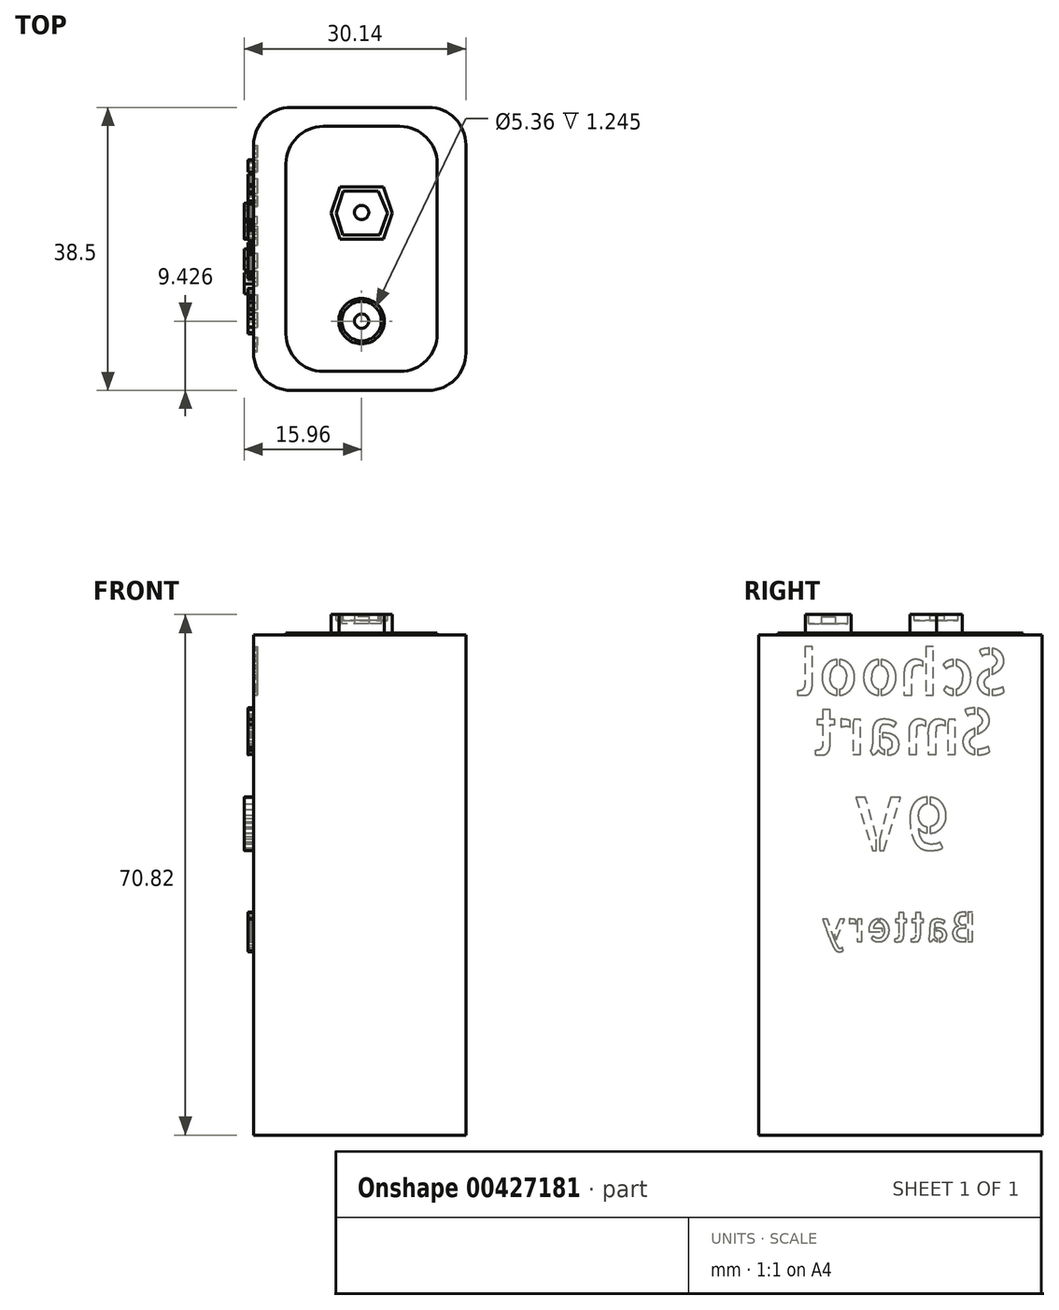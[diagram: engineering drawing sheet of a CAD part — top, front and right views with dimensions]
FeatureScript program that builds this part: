
annotation { "Feature Type Name" : "Feature", "Feature Type Description" : "" }
export const myFeature = defineFeature(function(context is Context, id is Id, definition is map)
    precondition{}
    {
        {
            var Q0;
            Q0=qCreatedBy(makeId("Top.planeOp"),FACE);
            var sketch = newSketch(context, id + "F0", { "sketchPlane" : qUnion([Q0])});
            skLineSegment(sketch, "E0.bottom", {"start": v(-14.18, 19.25) * mm, "end": v(14.18, 19.25) * mm});
            skLineSegment(sketch, "E0.top", {"start": v(-14.18, -19.25) * mm, "end": v(14.18, -19.25) * mm});
            skLineSegment(sketch, "E0.left", {"start": v(-14.18, 19.25) * mm, "end": v(-14.18, -19.25) * mm});
            skLineSegment(sketch, "E0.right", {"start": v(14.18, 19.25) * mm, "end": v(14.18, -19.25) * mm});
            skPoint(sketch, "E0.middle", {"position": v(0, 0) * mm});
            skSolve(sketch);
        }
        {
            var Q0;
            Q0=makeQuery(id+"F0.imprint","IMPRINT",FACE,{"disambiguationData":[TD([[makeQuery(id+"F0.imprint","IMPRINT",EDGE,{"derivedFrom":sQuery(id+"F0.wireOp",EDGE,"E0.bottom")}),-1.0]])]});
            extrude(context, id + "F1", {"entities" : qUnion([Q0]), "depth" : 68.07 * mm});
        }
        {
            var Q0;
            Q0=makeQuery(id+"F1.opExtrude","CAP_FACE",FACE,{"disambiguationData":[OSD([sQuery(id+"F0.wireOp",EDGE,"E0.bottom"),sQuery(id+"F0.wireOp",EDGE,"E0.top"),sQuery(id+"F0.wireOp",EDGE,"E0.left"),sQuery(id+"F0.wireOp",EDGE,"E0.right")])],"isStart":false});
            var sketch = newSketch(context, id + "F2", { "sketchPlane" : qUnion([Q0])});
            skLineSegment(sketch, "E1", {"start": v(0, 8.42) * mm, "end": v(-2.94, 8.42) * mm});
            skLineSegment(sketch, "E2", {"start": v(0, 8.42) * mm, "end": v(2.94, 8.42) * mm});
            skLineSegment(sketch, "E3", {"start": v(2.94, 8.42) * mm, "end": v(4.16, 4.9) * mm});
            skLineSegment(sketch, "E4", {"start": v(4.16, 4.9) * mm, "end": v(2.94, 1.33) * mm});
            skLineSegment(sketch, "E5", {"start": v(2.94, 1.33) * mm, "end": v(-2.94, 1.33) * mm});
            skLineSegment(sketch, "E6", {"start": v(-2.94, 1.33) * mm, "end": v(-4.16, 4.9) * mm});
            skLineSegment(sketch, "E7", {"start": v(-4.16, 4.9) * mm, "end": v(-2.94, 8.42) * mm});
            skSolve(sketch);
        }
        {
            var Q0;
            Q0=makeQuery(id+"F2.imprint","IMPRINT",FACE,{"disambiguationData":[TD([[makeQuery(id+"F2.imprint","IMPRINT",EDGE,{"derivedFrom":sQuery(id+"F2.wireOp",EDGE,"E1")}),1.0]])]});
            extrude(context, id + "F3", {"entities" : qUnion([Q0]), "operationType" : NewBodyOperationType.ADD, "depth" : 2.74 * mm});
        }
        {
            var Q0;
            Q0=makeQuery(id+"F3.opExtrude","CAP_FACE",FACE,{"disambiguationData":[OSD([sQuery(id+"F2.wireOp",EDGE,"E1"),sQuery(id+"F2.wireOp",EDGE,"E2"),sQuery(id+"F2.wireOp",EDGE,"E3"),sQuery(id+"F2.wireOp",EDGE,"E4"),sQuery(id+"F2.wireOp",EDGE,"E5"),sQuery(id+"F2.wireOp",EDGE,"E6"),sQuery(id+"F2.wireOp",EDGE,"E7")])],"isStart":false});
            var sketch = newSketch(context, id + "F4", { "sketchPlane" : qUnion([Q0])});
            skLineSegment(sketch, "E8", {"start": v(3.55, 4.9) * mm, "end": v(2.26, 7.85) * mm});
            skPoint(sketch, "E8.startSnap0", {"position": v(3.55, 6.66) * mm});
            skLineSegment(sketch, "E9", {"start": v(2.26, 7.85) * mm, "end": v(-2.5, 7.85) * mm});
            skLineSegment(sketch, "E10", {"start": v(-2.5, 7.85) * mm, "end": v(-3.49, 4.9) * mm});
            skLineSegment(sketch, "E11", {"start": v(-3.49, 4.9) * mm, "end": v(-2.6, 1.88) * mm});
            skLineSegment(sketch, "E12", {"start": v(-2.6, 1.88) * mm, "end": v(2.48, 1.88) * mm});
            skLineSegment(sketch, "E13", {"start": v(2.48, 1.88) * mm, "end": v(3.55, 4.9) * mm});
            skSolve(sketch);
        }
        {
            var Q0;
            Q0=makeQuery(id+"F4.imprint","IMPRINT",FACE,{"disambiguationData":[TD([[makeQuery(id+"F4.imprint","IMPRINT",EDGE,{"derivedFrom":sQuery(id+"F4.wireOp",EDGE,"E8")}),1.0]])]});
            extrude(context, id + "F5", {"entities" : qUnion([Q0]), "operationType" : NewBodyOperationType.REMOVE, "oppositeDirection" : true, "depth" : 1.07 * mm});
        }
        {
            var Q0;
            Q0=makeQuery(id+"F2.imprint","IMPRINT",FACE,{"disambiguationData":[TD([[makeQuery(id+"F2.imprint","IMPRINT",EDGE,{"derivedFrom":sQuery(id+"F2.wireOp",EDGE,"E1")}),-1.0]])]});
            var sketch = newSketch(context, id + "F6", { "sketchPlane" : qUnion([Q0])});
            skCircle(sketch, "E14", {"center": v(0, -9.82) * mm, "radius": 3.1 * mm});
            skSolve(sketch);
        }
        {
            var Q0;
            Q0=makeQuery(id+"F6.imprint","IMPRINT",FACE,{"disambiguationData":[TD([[makeQuery(id+"F6.imprint","IMPRINT",EDGE,{"derivedFrom":sQuery(id+"F6.wireOp",EDGE,"E14")}),1.0]])]});
            var Q1;
            Q1=sQuery(id+"F6.wireOp",EDGE,"E14");
            extrude(context, id + "F7", {"entities" : qUnion([Q0]), "operationType" : NewBodyOperationType.ADD, "surfaceEntities" : qUnion([Q1]), "depth" : 2.74 * mm});
        }
        {
            var Q0;
            Q0=makeQuery(id+"F7.opExtrude","CAP_FACE",FACE,{"disambiguationData":[OSD([sQuery(id+"F6.wireOp",EDGE,"E14")])],"isStart":false});
            var sketch = newSketch(context, id + "F8", { "sketchPlane" : qUnion([Q0])});
            skCircle(sketch, "E15", {"center": v(0, -9.82) * mm, "radius": 2.68 * mm});
            skSolve(sketch);
        }
        {
            var Q0;
            Q0=makeQuery(id+"F8.imprint","IMPRINT",FACE,{"disambiguationData":[TD([[makeQuery(id+"F8.imprint","IMPRINT",EDGE,{"derivedFrom":sQuery(id+"F8.wireOp",EDGE,"E15")}),1.0]])]});
            extrude(context, id + "F9", {"entities" : qUnion([Q0]), "operationType" : NewBodyOperationType.REMOVE, "oppositeDirection" : true, "depth" : 1.24 * mm});
        }
        {
            var Q0;
            Q0=makeQuery(id+"F9.boolean.opBoolean","COPY",FACE,{"derivedFrom":makeQuery(id+"F9.opExtrude","CAP_FACE",FACE,{"disambiguationData":[OSD([sQuery(id+"F8.wireOp",EDGE,"E15")])],"isStart":false})});
            var sketch = newSketch(context, id + "F10", { "sketchPlane" : qUnion([Q0])});
            skCircle(sketch, "E16", {"center": v(0, -9.82) * mm, "radius": 0.97 * mm});
            skSolve(sketch);
        }
        {
            var Q0;
            Q0=makeQuery(id+"F10.imprint","IMPRINT",FACE,{"disambiguationData":[TD([[makeQuery(id+"F10.imprint","IMPRINT",EDGE,{"derivedFrom":sQuery(id+"F10.wireOp",EDGE,"E16")}),1.0]])]});
            extrude(context, id + "F11", {"entities" : qUnion([Q0]), "operationType" : NewBodyOperationType.ADD, "depth" : 0.94 * mm});
        }
        {
            var Q0;
            Q0=makeQuery(id+"F5.boolean.opBoolean","COPY",FACE,{"derivedFrom":makeQuery(id+"F5.opExtrude","CAP_FACE",FACE,{"disambiguationData":[OSD([sQuery(id+"F4.wireOp",EDGE,"E8"),sQuery(id+"F4.wireOp",EDGE,"E9"),sQuery(id+"F4.wireOp",EDGE,"E10"),sQuery(id+"F4.wireOp",EDGE,"E11"),sQuery(id+"F4.wireOp",EDGE,"E12"),sQuery(id+"F4.wireOp",EDGE,"E13")])],"isStart":false})});
            var sketch = newSketch(context, id + "F12", { "sketchPlane" : qUnion([Q0])});
            skCircle(sketch, "E17", {"center": v(0, 4.96) * mm, "radius": 0.97 * mm});
            skSolve(sketch);
        }
        {
            var Q0;
            Q0=makeQuery(id+"F12.imprint","IMPRINT",FACE,{"disambiguationData":[TD([[makeQuery(id+"F12.imprint","IMPRINT",EDGE,{"derivedFrom":sQuery(id+"F12.wireOp",EDGE,"E17")}),1.0]])]});
            extrude(context, id + "F13", {"entities" : qUnion([Q0]), "operationType" : NewBodyOperationType.ADD, "depth" : 0.94 * mm});
        }
        {
            var Q0;
            Q0=makeQuery(id+"F1.opExtrude","SWEPT_FACE",FACE,{"disambiguationData":[OSD([sQuery(id+"F0.wireOp",EDGE,"E0.left")])]});
            var sketch = newSketch(context, id + "F14", { "sketchPlane" : qUnion([Q0])});
            skText(sketch, "E18", { "text": "School", "fontName": "AllertaStencil-Regular.ttf"});
            const initialGuessF14  = {"E18": [-0.0148, 0.05987, 1, 0, 0.00628]};
            skSetInitialGuess(sketch, initialGuessF14);
            skSolve(sketch);
        }
        {
            var Q0;
            Q0=makeQuery(id+"F14.imprint","IMPRINT",FACE,{"disambiguationData":[TD([[makeQuery(id+"F14.imprint","IMPRINT",EDGE,{"derivedFrom":sQuery(id+"F14.wireOp",EDGE,"E18.sketch_text.stroke-0")}),1.0]])]});
            extrude(context, id + "F15", {"entities" : qUnion([Q0]), "operationType" : NewBodyOperationType.ADD, "depth" : 0.5 * mm});
        }
        {
            var Q0;
            Q0=makeQuery(id+"F15.opExtrude","CAP_FACE",FACE,{"disambiguationData":[OSD([sQuery(id+"F0.wireOp",EDGE,"E0.bottom"),sQuery(id+"F0.wireOp",EDGE,"E0.top"),sQuery(id+"F0.wireOp",EDGE,"E0.left"),sQuery(id+"F14.wireOp",EDGE,"E18.sketch_text.stroke-0"),sQuery(id+"F14.wireOp",EDGE,"E18.sketch_text.stroke-1"),sQuery(id+"F14.wireOp",EDGE,"E18.sketch_text.stroke-2"),sQuery(id+"F14.wireOp",EDGE,"E18.sketch_text.stroke-3"),sQuery(id+"F14.wireOp",EDGE,"E18.sketch_text.stroke-4"),sQuery(id+"F14.wireOp",EDGE,"E18.sketch_text.stroke-5"),sQuery(id+"F14.wireOp",EDGE,"E18.sketch_text.stroke-6"),sQuery(id+"F14.wireOp",EDGE,"E18.sketch_text.stroke-7"),sQuery(id+"F14.wireOp",EDGE,"E18.sketch_text.stroke-8"),sQuery(id+"F14.wireOp",EDGE,"E18.sketch_text.stroke-9"),sQuery(id+"F14.wireOp",EDGE,"E18.sketch_text.stroke-10"),sQuery(id+"F14.wireOp",EDGE,"E18.sketch_text.stroke-11"),sQuery(id+"F14.wireOp",EDGE,"E18.sketch_text.stroke-12"),sQuery(id+"F14.wireOp",EDGE,"E18.sketch_text.stroke-13"),sQuery(id+"F14.wireOp",EDGE,"E18.sketch_text.stroke-14"),sQuery(id+"F14.wireOp",EDGE,"E18.sketch_text.stroke-15"),sQuery(id+"F14.wireOp",EDGE,"E18.sketch_text.stroke-16"),sQuery(id+"F14.wireOp",EDGE,"E18.sketch_text.stroke-17"),sQuery(id+"F14.wireOp",EDGE,"E18.sketch_text.stroke-18"),sQuery(id+"F14.wireOp",EDGE,"E18.sketch_text.stroke-19"),sQuery(id+"F14.wireOp",EDGE,"E18.sketch_text.stroke-20"),sQuery(id+"F14.wireOp",EDGE,"E18.sketch_text.stroke-21"),sQuery(id+"F14.wireOp",EDGE,"E18.sketch_text.stroke-22"),sQuery(id+"F14.wireOp",EDGE,"E18.sketch_text.stroke-23"),sQuery(id+"F14.wireOp",EDGE,"E18.sketch_text.stroke-24"),sQuery(id+"F14.wireOp",EDGE,"E18.sketch_text.stroke-25"),sQuery(id+"F14.wireOp",EDGE,"E18.sketch_text.stroke-26"),sQuery(id+"F14.wireOp",EDGE,"E18.sketch_text.stroke-27"),sQuery(id+"F14.wireOp",EDGE,"E18.sketch_text.stroke-28"),sQuery(id+"F14.wireOp",EDGE,"E18.sketch_text.stroke-29"),sQuery(id+"F14.wireOp",EDGE,"E18.sketch_text.stroke-30"),sQuery(id+"F14.wireOp",EDGE,"E18.sketch_text.stroke-31"),sQuery(id+"F14.wireOp",EDGE,"E18.sketch_text.stroke-32"),sQuery(id+"F14.wireOp",EDGE,"E18.sketch_text.stroke-33"),sQuery(id+"F14.wireOp",EDGE,"E18.sketch_text.stroke-34"),sQuery(id+"F14.wireOp",EDGE,"E18.sketch_text.stroke-35"),sQuery(id+"F14.wireOp",EDGE,"E18.sketch_text.stroke-36"),sQuery(id+"F14.wireOp",EDGE,"E18.sketch_text.stroke-37"),sQuery(id+"F14.wireOp",EDGE,"E18.sketch_text.stroke-38"),sQuery(id+"F14.wireOp",EDGE,"E18.sketch_text.stroke-39"),sQuery(id+"F14.wireOp",EDGE,"E18.sketch_text.stroke-40"),sQuery(id+"F14.wireOp",EDGE,"E18.sketch_text.stroke-41"),sQuery(id+"F14.wireOp",EDGE,"E18.sketch_text.stroke-42"),sQuery(id+"F14.wireOp",EDGE,"E18.sketch_text.stroke-43"),sQuery(id+"F14.wireOp",EDGE,"E18.sketch_text.stroke-44"),sQuery(id+"F14.wireOp",EDGE,"E18.sketch_text.stroke-45"),sQuery(id+"F14.wireOp",EDGE,"E18.sketch_text.stroke-46"),sQuery(id+"F14.wireOp",EDGE,"E18.sketch_text.stroke-47"),sQuery(id+"F14.wireOp",EDGE,"E18.sketch_text.stroke-48"),sQuery(id+"F14.wireOp",EDGE,"E18.sketch_text.stroke-49"),sQuery(id+"F14.wireOp",EDGE,"E18.sketch_text.stroke-50"),sQuery(id+"F14.wireOp",EDGE,"E18.sketch_text.stroke-51"),sQuery(id+"F14.wireOp",EDGE,"E18.sketch_text.stroke-52"),sQuery(id+"F14.wireOp",EDGE,"E18.sketch_text.stroke-53"),sQuery(id+"F14.wireOp",EDGE,"E18.sketch_text.stroke-54"),sQuery(id+"F14.wireOp",EDGE,"E18.sketch_text.stroke-55"),sQuery(id+"F14.wireOp",EDGE,"E18.sketch_text.stroke-56"),sQuery(id+"F14.wireOp",EDGE,"E18.sketch_text.stroke-57"),sQuery(id+"F14.wireOp",EDGE,"E18.sketch_text.stroke-58"),sQuery(id+"F14.wireOp",EDGE,"E18.sketch_text.stroke-59"),sQuery(id+"F14.wireOp",EDGE,"E18.sketch_text.stroke-60"),sQuery(id+"F14.wireOp",EDGE,"E18.sketch_text.stroke-61"),sQuery(id+"F14.wireOp",EDGE,"E18.sketch_text.stroke-62"),sQuery(id+"F14.wireOp",EDGE,"E18.sketch_text.stroke-63"),sQuery(id+"F14.wireOp",EDGE,"E18.sketch_text.stroke-64"),sQuery(id+"F14.wireOp",EDGE,"E18.sketch_text.stroke-65"),sQuery(id+"F14.wireOp",EDGE,"E18.sketch_text.stroke-66"),sQuery(id+"F14.wireOp",EDGE,"E18.sketch_text.stroke-67"),sQuery(id+"F14.wireOp",EDGE,"E18.sketch_text.stroke-68"),sQuery(id+"F14.wireOp",EDGE,"E18.sketch_text.stroke-69"),sQuery(id+"F14.wireOp",EDGE,"E18.sketch_text.stroke-70"),sQuery(id+"F14.wireOp",EDGE,"E18.sketch_text.stroke-71"),sQuery(id+"F14.wireOp",EDGE,"E18.sketch_text.stroke-72"),sQuery(id+"F14.wireOp",EDGE,"E18.sketch_text.stroke-73"),sQuery(id+"F14.wireOp",EDGE,"E18.sketch_text.stroke-74"),sQuery(id+"F14.wireOp",EDGE,"E18.sketch_text.stroke-75"),sQuery(id+"F14.wireOp",EDGE,"E18.sketch_text.stroke-76"),sQuery(id+"F14.wireOp",EDGE,"E18.sketch_text.stroke-77"),sQuery(id+"F14.wireOp",EDGE,"E18.sketch_text.stroke-78"),sQuery(id+"F14.wireOp",EDGE,"E18.sketch_text.stroke-79"),sQuery(id+"F14.wireOp",EDGE,"E18.sketch_text.stroke-80"),sQuery(id+"F14.wireOp",EDGE,"E18.sketch_text.stroke-81"),sQuery(id+"F14.wireOp",EDGE,"E18.sketch_text.stroke-82"),sQuery(id+"F14.wireOp",EDGE,"E18.sketch_text.stroke-83"),sQuery(id+"F14.wireOp",EDGE,"E18.sketch_text.stroke-84"),sQuery(id+"F14.wireOp",EDGE,"E18.sketch_text.stroke-85"),sQuery(id+"F14.wireOp",EDGE,"E18.sketch_text.stroke-86"),sQuery(id+"F14.wireOp",EDGE,"E18.sketch_text.stroke-87"),sQuery(id+"F14.wireOp",EDGE,"E18.sketch_text.stroke-88"),sQuery(id+"F14.wireOp",EDGE,"E18.sketch_text.stroke-89"),sQuery(id+"F14.wireOp",EDGE,"E18.sketch_text.stroke-90"),sQuery(id+"F14.wireOp",EDGE,"E18.sketch_text.stroke-91"),sQuery(id+"F14.wireOp",EDGE,"E18.sketch_text.stroke-92"),sQuery(id+"F14.wireOp",EDGE,"E18.sketch_text.stroke-93"),sQuery(id+"F14.wireOp",EDGE,"E18.sketch_text.stroke-94"),sQuery(id+"F14.wireOp",EDGE,"E18.sketch_text.stroke-95"),sQuery(id+"F14.wireOp",EDGE,"E18.sketch_text.stroke-96"),sQuery(id+"F14.wireOp",EDGE,"E18.sketch_text.stroke-97"),sQuery(id+"F14.wireOp",EDGE,"E18.sketch_text.stroke-98"),sQuery(id+"F14.wireOp",EDGE,"E18.sketch_text.stroke-99"),sQuery(id+"F14.wireOp",EDGE,"E18.sketch_text.stroke-100"),sQuery(id+"F14.wireOp",EDGE,"E18.sketch_text.stroke-101"),sQuery(id+"F14.wireOp",EDGE,"E18.sketch_text.stroke-102"),sQuery(id+"F14.wireOp",EDGE,"E18.sketch_text.stroke-103"),sQuery(id+"F14.wireOp",EDGE,"E18.sketch_text.stroke-104"),sQuery(id+"F14.wireOp",EDGE,"E18.sketch_text.stroke-105"),sQuery(id+"F14.wireOp",EDGE,"E18.sketch_text.stroke-106"),sQuery(id+"F14.wireOp",EDGE,"E18.sketch_text.stroke-107"),sQuery(id+"F14.wireOp",EDGE,"E18.sketch_text.stroke-108"),sQuery(id+"F14.wireOp",EDGE,"E18.sketch_text.stroke-109"),sQuery(id+"F14.wireOp",EDGE,"E18.sketch_text.stroke-110"),sQuery(id+"F14.wireOp",EDGE,"E18.sketch_text.stroke-111"),sQuery(id+"F14.wireOp",EDGE,"E18.sketch_text.stroke-112"),sQuery(id+"F14.wireOp",EDGE,"E18.sketch_text.stroke-113"),sQuery(id+"F14.wireOp",EDGE,"E18.sketch_text.stroke-114"),sQuery(id+"F14.wireOp",EDGE,"E18.sketch_text.stroke-115"),sQuery(id+"F14.wireOp",EDGE,"E18.sketch_text.stroke-116"),sQuery(id+"F14.wireOp",EDGE,"E18.sketch_text.stroke-117"),sQuery(id+"F14.wireOp",EDGE,"E18.sketch_text.stroke-118"),sQuery(id+"F14.wireOp",EDGE,"E18.sketch_text.stroke-119"),sQuery(id+"F14.wireOp",EDGE,"E18.sketch_text.stroke-120"),sQuery(id+"F14.wireOp",EDGE,"E18.sketch_text.stroke-121"),sQuery(id+"F14.wireOp",EDGE,"E18.sketch_text.stroke-122"),sQuery(id+"F14.wireOp",EDGE,"E18.sketch_text.stroke-123"),sQuery(id+"F14.wireOp",EDGE,"E18.sketch_text.stroke-124"),sQuery(id+"F14.wireOp",EDGE,"E18.sketch_text.stroke-125"),sQuery(id+"F14.wireOp",EDGE,"E18.sketch_text.stroke-126"),sQuery(id+"F14.wireOp",EDGE,"E18.sketch_text.stroke-127"),sQuery(id+"F14.wireOp",EDGE,"E18.sketch_text.stroke-128"),sQuery(id+"F14.wireOp",EDGE,"E18.sketch_text.stroke-129"),sQuery(id+"F14.wireOp",EDGE,"E18.sketch_text.stroke-130"),sQuery(id+"F14.wireOp",EDGE,"E18.sketch_text.stroke-131"),sQuery(id+"F14.wireOp",EDGE,"E18.sketch_text.stroke-132"),sQuery(id+"F14.wireOp",EDGE,"E18.sketch_text.stroke-133"),sQuery(id+"F14.wireOp",EDGE,"E18.sketch_text.stroke-134"),sQuery(id+"F14.wireOp",EDGE,"E18.sketch_text.stroke-135"),sQuery(id+"F14.wireOp",EDGE,"E18.sketch_text.stroke-136"),sQuery(id+"F14.wireOp",EDGE,"E18.sketch_text.stroke-137"),sQuery(id+"F14.wireOp",EDGE,"E18.sketch_text.stroke-138"),sQuery(id+"F14.wireOp",EDGE,"E18.sketch_text.stroke-139"),sQuery(id+"F14.wireOp",EDGE,"E18.sketch_text.stroke-140"),sQuery(id+"F14.wireOp",EDGE,"E18.sketch_text.stroke-141"),sQuery(id+"F14.wireOp",EDGE,"E18.sketch_text.stroke-142"),sQuery(id+"F14.wireOp",EDGE,"E18.sketch_text.stroke-143"),sQuery(id+"F14.wireOp",EDGE,"E18.sketch_text.stroke-144"),sQuery(id+"F14.wireOp",EDGE,"E18.sketch_text.stroke-145"),sQuery(id+"F14.wireOp",EDGE,"E18.sketch_text.stroke-146"),sQuery(id+"F14.wireOp",EDGE,"E18.sketch_text.stroke-147"),sQuery(id+"F14.wireOp",EDGE,"E18.sketch_text.stroke-148"),sQuery(id+"F14.wireOp",EDGE,"E18.sketch_text.stroke-149"),sQuery(id+"F14.wireOp",EDGE,"E18.sketch_text.stroke-150"),sQuery(id+"F14.wireOp",EDGE,"E18.sketch_text.stroke-151"),sQuery(id+"F14.wireOp",EDGE,"E18.sketch_text.stroke-152"),sQuery(id+"F14.wireOp",EDGE,"E18.sketch_text.stroke-153"),sQuery(id+"F14.wireOp",EDGE,"E18.sketch_text.stroke-154"),sQuery(id+"F14.wireOp",EDGE,"E18.sketch_text.stroke-155"),sQuery(id+"F14.wireOp",EDGE,"E18.sketch_text.stroke-156"),sQuery(id+"F14.wireOp",EDGE,"E18.sketch_text.stroke-157"),sQuery(id+"F14.wireOp",EDGE,"E18.sketch_text.stroke-158"),sQuery(id+"F14.wireOp",EDGE,"E18.sketch_text.stroke-159"),sQuery(id+"F14.wireOp",EDGE,"E18.sketch_text.stroke-160"),sQuery(id+"F14.wireOp",EDGE,"E18.sketch_text.stroke-161"),sQuery(id+"F14.wireOp",EDGE,"E18.sketch_text.stroke-162"),sQuery(id+"F14.wireOp",EDGE,"E18.sketch_text.stroke-163"),sQuery(id+"F14.wireOp",EDGE,"E18.sketch_text.stroke-164"),sQuery(id+"F14.wireOp",EDGE,"E18.sketch_text.stroke-165"),sQuery(id+"F14.wireOp",EDGE,"E18.sketch_text.stroke-166"),sQuery(id+"F14.wireOp",EDGE,"E18.sketch_text.stroke-167"),sQuery(id+"F14.wireOp",EDGE,"E18.sketch_text.stroke-168"),sQuery(id+"F14.wireOp",EDGE,"E18.sketch_text.stroke-169"),sQuery(id+"F14.wireOp",EDGE,"E18.sketch_text.stroke-170"),sQuery(id+"F14.wireOp",EDGE,"E18.sketch_text.stroke-171"),sQuery(id+"F14.wireOp",EDGE,"E18.sketch_text.stroke-172"),sQuery(id+"F14.wireOp",EDGE,"E18.sketch_text.stroke-173"),sQuery(id+"F14.wireOp",EDGE,"E18.sketch_text.stroke-174"),sQuery(id+"F14.wireOp",EDGE,"E18.sketch_text.stroke-175"),sQuery(id+"F14.wireOp",EDGE,"E18.sketch_text.stroke-176"),sQuery(id+"F14.wireOp",EDGE,"E18.sketch_text.stroke-177"),sQuery(id+"F14.wireOp",EDGE,"E18.sketch_text.stroke-178"),sQuery(id+"F14.wireOp",EDGE,"E18.sketch_text.stroke-179"),sQuery(id+"F14.wireOp",EDGE,"E18.sketch_text.stroke-180"),sQuery(id+"F14.wireOp",EDGE,"E18.sketch_text.stroke-181"),sQuery(id+"F14.wireOp",EDGE,"E18.sketch_text.stroke-182")])],"isStart":false});
            var sketch = newSketch(context, id + "F16", { "sketchPlane" : qUnion([Q0])});
            skText(sketch, "E19", { "text": "Smart", "fontName": "AllertaStencil-Regular.ttf"});
            const initialGuessF16  = {"E19": [-0.01282, 0.05176, 1, 0, 0.00627]};
            skSetInitialGuess(sketch, initialGuessF16);
            skSolve(sketch);
        }
        {
            var Q0;
            Q0 = qSketchRegion(id + "F16", true);
            extrude(context, id + "F17", {"entities" : qUnion([Q0]), "operationType" : NewBodyOperationType.ADD, "depth" : 0.76 * mm});
        }
        {
            var Q0;
            Q0=makeQuery(id+"F15.opExtrude","CAP_FACE",FACE,{"disambiguationData":[OSD([sQuery(id+"F0.wireOp",EDGE,"E0.bottom"),sQuery(id+"F0.wireOp",EDGE,"E0.top"),sQuery(id+"F0.wireOp",EDGE,"E0.left"),sQuery(id+"F14.wireOp",EDGE,"E18.sketch_text.stroke-0"),sQuery(id+"F14.wireOp",EDGE,"E18.sketch_text.stroke-1"),sQuery(id+"F14.wireOp",EDGE,"E18.sketch_text.stroke-2"),sQuery(id+"F14.wireOp",EDGE,"E18.sketch_text.stroke-3"),sQuery(id+"F14.wireOp",EDGE,"E18.sketch_text.stroke-4"),sQuery(id+"F14.wireOp",EDGE,"E18.sketch_text.stroke-5"),sQuery(id+"F14.wireOp",EDGE,"E18.sketch_text.stroke-6"),sQuery(id+"F14.wireOp",EDGE,"E18.sketch_text.stroke-7"),sQuery(id+"F14.wireOp",EDGE,"E18.sketch_text.stroke-8"),sQuery(id+"F14.wireOp",EDGE,"E18.sketch_text.stroke-9"),sQuery(id+"F14.wireOp",EDGE,"E18.sketch_text.stroke-10"),sQuery(id+"F14.wireOp",EDGE,"E18.sketch_text.stroke-11"),sQuery(id+"F14.wireOp",EDGE,"E18.sketch_text.stroke-12"),sQuery(id+"F14.wireOp",EDGE,"E18.sketch_text.stroke-13"),sQuery(id+"F14.wireOp",EDGE,"E18.sketch_text.stroke-14"),sQuery(id+"F14.wireOp",EDGE,"E18.sketch_text.stroke-15"),sQuery(id+"F14.wireOp",EDGE,"E18.sketch_text.stroke-16"),sQuery(id+"F14.wireOp",EDGE,"E18.sketch_text.stroke-17"),sQuery(id+"F14.wireOp",EDGE,"E18.sketch_text.stroke-18"),sQuery(id+"F14.wireOp",EDGE,"E18.sketch_text.stroke-19"),sQuery(id+"F14.wireOp",EDGE,"E18.sketch_text.stroke-20"),sQuery(id+"F14.wireOp",EDGE,"E18.sketch_text.stroke-21"),sQuery(id+"F14.wireOp",EDGE,"E18.sketch_text.stroke-22"),sQuery(id+"F14.wireOp",EDGE,"E18.sketch_text.stroke-23"),sQuery(id+"F14.wireOp",EDGE,"E18.sketch_text.stroke-24"),sQuery(id+"F14.wireOp",EDGE,"E18.sketch_text.stroke-25"),sQuery(id+"F14.wireOp",EDGE,"E18.sketch_text.stroke-26"),sQuery(id+"F14.wireOp",EDGE,"E18.sketch_text.stroke-27"),sQuery(id+"F14.wireOp",EDGE,"E18.sketch_text.stroke-28"),sQuery(id+"F14.wireOp",EDGE,"E18.sketch_text.stroke-29"),sQuery(id+"F14.wireOp",EDGE,"E18.sketch_text.stroke-30"),sQuery(id+"F14.wireOp",EDGE,"E18.sketch_text.stroke-31"),sQuery(id+"F14.wireOp",EDGE,"E18.sketch_text.stroke-32"),sQuery(id+"F14.wireOp",EDGE,"E18.sketch_text.stroke-33"),sQuery(id+"F14.wireOp",EDGE,"E18.sketch_text.stroke-34"),sQuery(id+"F14.wireOp",EDGE,"E18.sketch_text.stroke-35"),sQuery(id+"F14.wireOp",EDGE,"E18.sketch_text.stroke-36"),sQuery(id+"F14.wireOp",EDGE,"E18.sketch_text.stroke-37"),sQuery(id+"F14.wireOp",EDGE,"E18.sketch_text.stroke-38"),sQuery(id+"F14.wireOp",EDGE,"E18.sketch_text.stroke-39"),sQuery(id+"F14.wireOp",EDGE,"E18.sketch_text.stroke-40"),sQuery(id+"F14.wireOp",EDGE,"E18.sketch_text.stroke-41"),sQuery(id+"F14.wireOp",EDGE,"E18.sketch_text.stroke-42"),sQuery(id+"F14.wireOp",EDGE,"E18.sketch_text.stroke-43"),sQuery(id+"F14.wireOp",EDGE,"E18.sketch_text.stroke-44"),sQuery(id+"F14.wireOp",EDGE,"E18.sketch_text.stroke-45"),sQuery(id+"F14.wireOp",EDGE,"E18.sketch_text.stroke-46"),sQuery(id+"F14.wireOp",EDGE,"E18.sketch_text.stroke-47"),sQuery(id+"F14.wireOp",EDGE,"E18.sketch_text.stroke-48"),sQuery(id+"F14.wireOp",EDGE,"E18.sketch_text.stroke-49"),sQuery(id+"F14.wireOp",EDGE,"E18.sketch_text.stroke-50"),sQuery(id+"F14.wireOp",EDGE,"E18.sketch_text.stroke-51"),sQuery(id+"F14.wireOp",EDGE,"E18.sketch_text.stroke-52"),sQuery(id+"F14.wireOp",EDGE,"E18.sketch_text.stroke-53"),sQuery(id+"F14.wireOp",EDGE,"E18.sketch_text.stroke-54"),sQuery(id+"F14.wireOp",EDGE,"E18.sketch_text.stroke-55"),sQuery(id+"F14.wireOp",EDGE,"E18.sketch_text.stroke-56"),sQuery(id+"F14.wireOp",EDGE,"E18.sketch_text.stroke-57"),sQuery(id+"F14.wireOp",EDGE,"E18.sketch_text.stroke-58"),sQuery(id+"F14.wireOp",EDGE,"E18.sketch_text.stroke-59"),sQuery(id+"F14.wireOp",EDGE,"E18.sketch_text.stroke-60"),sQuery(id+"F14.wireOp",EDGE,"E18.sketch_text.stroke-61"),sQuery(id+"F14.wireOp",EDGE,"E18.sketch_text.stroke-62"),sQuery(id+"F14.wireOp",EDGE,"E18.sketch_text.stroke-63"),sQuery(id+"F14.wireOp",EDGE,"E18.sketch_text.stroke-64"),sQuery(id+"F14.wireOp",EDGE,"E18.sketch_text.stroke-65"),sQuery(id+"F14.wireOp",EDGE,"E18.sketch_text.stroke-66"),sQuery(id+"F14.wireOp",EDGE,"E18.sketch_text.stroke-67"),sQuery(id+"F14.wireOp",EDGE,"E18.sketch_text.stroke-68"),sQuery(id+"F14.wireOp",EDGE,"E18.sketch_text.stroke-69"),sQuery(id+"F14.wireOp",EDGE,"E18.sketch_text.stroke-70"),sQuery(id+"F14.wireOp",EDGE,"E18.sketch_text.stroke-71"),sQuery(id+"F14.wireOp",EDGE,"E18.sketch_text.stroke-72"),sQuery(id+"F14.wireOp",EDGE,"E18.sketch_text.stroke-73"),sQuery(id+"F14.wireOp",EDGE,"E18.sketch_text.stroke-74"),sQuery(id+"F14.wireOp",EDGE,"E18.sketch_text.stroke-75"),sQuery(id+"F14.wireOp",EDGE,"E18.sketch_text.stroke-76"),sQuery(id+"F14.wireOp",EDGE,"E18.sketch_text.stroke-77"),sQuery(id+"F14.wireOp",EDGE,"E18.sketch_text.stroke-78"),sQuery(id+"F14.wireOp",EDGE,"E18.sketch_text.stroke-79"),sQuery(id+"F14.wireOp",EDGE,"E18.sketch_text.stroke-80"),sQuery(id+"F14.wireOp",EDGE,"E18.sketch_text.stroke-81"),sQuery(id+"F14.wireOp",EDGE,"E18.sketch_text.stroke-82"),sQuery(id+"F14.wireOp",EDGE,"E18.sketch_text.stroke-83"),sQuery(id+"F14.wireOp",EDGE,"E18.sketch_text.stroke-84"),sQuery(id+"F14.wireOp",EDGE,"E18.sketch_text.stroke-85"),sQuery(id+"F14.wireOp",EDGE,"E18.sketch_text.stroke-86"),sQuery(id+"F14.wireOp",EDGE,"E18.sketch_text.stroke-87"),sQuery(id+"F14.wireOp",EDGE,"E18.sketch_text.stroke-88"),sQuery(id+"F14.wireOp",EDGE,"E18.sketch_text.stroke-89"),sQuery(id+"F14.wireOp",EDGE,"E18.sketch_text.stroke-90"),sQuery(id+"F14.wireOp",EDGE,"E18.sketch_text.stroke-91"),sQuery(id+"F14.wireOp",EDGE,"E18.sketch_text.stroke-92"),sQuery(id+"F14.wireOp",EDGE,"E18.sketch_text.stroke-93"),sQuery(id+"F14.wireOp",EDGE,"E18.sketch_text.stroke-94"),sQuery(id+"F14.wireOp",EDGE,"E18.sketch_text.stroke-95"),sQuery(id+"F14.wireOp",EDGE,"E18.sketch_text.stroke-96"),sQuery(id+"F14.wireOp",EDGE,"E18.sketch_text.stroke-97"),sQuery(id+"F14.wireOp",EDGE,"E18.sketch_text.stroke-98"),sQuery(id+"F14.wireOp",EDGE,"E18.sketch_text.stroke-99"),sQuery(id+"F14.wireOp",EDGE,"E18.sketch_text.stroke-100"),sQuery(id+"F14.wireOp",EDGE,"E18.sketch_text.stroke-101"),sQuery(id+"F14.wireOp",EDGE,"E18.sketch_text.stroke-102"),sQuery(id+"F14.wireOp",EDGE,"E18.sketch_text.stroke-103"),sQuery(id+"F14.wireOp",EDGE,"E18.sketch_text.stroke-104"),sQuery(id+"F14.wireOp",EDGE,"E18.sketch_text.stroke-105"),sQuery(id+"F14.wireOp",EDGE,"E18.sketch_text.stroke-106"),sQuery(id+"F14.wireOp",EDGE,"E18.sketch_text.stroke-107"),sQuery(id+"F14.wireOp",EDGE,"E18.sketch_text.stroke-108"),sQuery(id+"F14.wireOp",EDGE,"E18.sketch_text.stroke-109"),sQuery(id+"F14.wireOp",EDGE,"E18.sketch_text.stroke-110"),sQuery(id+"F14.wireOp",EDGE,"E18.sketch_text.stroke-111"),sQuery(id+"F14.wireOp",EDGE,"E18.sketch_text.stroke-112"),sQuery(id+"F14.wireOp",EDGE,"E18.sketch_text.stroke-113"),sQuery(id+"F14.wireOp",EDGE,"E18.sketch_text.stroke-114"),sQuery(id+"F14.wireOp",EDGE,"E18.sketch_text.stroke-115"),sQuery(id+"F14.wireOp",EDGE,"E18.sketch_text.stroke-116"),sQuery(id+"F14.wireOp",EDGE,"E18.sketch_text.stroke-117"),sQuery(id+"F14.wireOp",EDGE,"E18.sketch_text.stroke-118"),sQuery(id+"F14.wireOp",EDGE,"E18.sketch_text.stroke-119"),sQuery(id+"F14.wireOp",EDGE,"E18.sketch_text.stroke-120"),sQuery(id+"F14.wireOp",EDGE,"E18.sketch_text.stroke-121"),sQuery(id+"F14.wireOp",EDGE,"E18.sketch_text.stroke-122"),sQuery(id+"F14.wireOp",EDGE,"E18.sketch_text.stroke-123"),sQuery(id+"F14.wireOp",EDGE,"E18.sketch_text.stroke-124"),sQuery(id+"F14.wireOp",EDGE,"E18.sketch_text.stroke-125"),sQuery(id+"F14.wireOp",EDGE,"E18.sketch_text.stroke-126"),sQuery(id+"F14.wireOp",EDGE,"E18.sketch_text.stroke-127"),sQuery(id+"F14.wireOp",EDGE,"E18.sketch_text.stroke-128"),sQuery(id+"F14.wireOp",EDGE,"E18.sketch_text.stroke-129"),sQuery(id+"F14.wireOp",EDGE,"E18.sketch_text.stroke-130"),sQuery(id+"F14.wireOp",EDGE,"E18.sketch_text.stroke-131"),sQuery(id+"F14.wireOp",EDGE,"E18.sketch_text.stroke-132"),sQuery(id+"F14.wireOp",EDGE,"E18.sketch_text.stroke-133"),sQuery(id+"F14.wireOp",EDGE,"E18.sketch_text.stroke-134"),sQuery(id+"F14.wireOp",EDGE,"E18.sketch_text.stroke-135"),sQuery(id+"F14.wireOp",EDGE,"E18.sketch_text.stroke-136"),sQuery(id+"F14.wireOp",EDGE,"E18.sketch_text.stroke-137"),sQuery(id+"F14.wireOp",EDGE,"E18.sketch_text.stroke-138"),sQuery(id+"F14.wireOp",EDGE,"E18.sketch_text.stroke-139"),sQuery(id+"F14.wireOp",EDGE,"E18.sketch_text.stroke-140"),sQuery(id+"F14.wireOp",EDGE,"E18.sketch_text.stroke-141"),sQuery(id+"F14.wireOp",EDGE,"E18.sketch_text.stroke-142"),sQuery(id+"F14.wireOp",EDGE,"E18.sketch_text.stroke-143"),sQuery(id+"F14.wireOp",EDGE,"E18.sketch_text.stroke-144"),sQuery(id+"F14.wireOp",EDGE,"E18.sketch_text.stroke-145"),sQuery(id+"F14.wireOp",EDGE,"E18.sketch_text.stroke-146"),sQuery(id+"F14.wireOp",EDGE,"E18.sketch_text.stroke-147"),sQuery(id+"F14.wireOp",EDGE,"E18.sketch_text.stroke-148"),sQuery(id+"F14.wireOp",EDGE,"E18.sketch_text.stroke-149"),sQuery(id+"F14.wireOp",EDGE,"E18.sketch_text.stroke-150"),sQuery(id+"F14.wireOp",EDGE,"E18.sketch_text.stroke-151"),sQuery(id+"F14.wireOp",EDGE,"E18.sketch_text.stroke-152"),sQuery(id+"F14.wireOp",EDGE,"E18.sketch_text.stroke-153"),sQuery(id+"F14.wireOp",EDGE,"E18.sketch_text.stroke-154"),sQuery(id+"F14.wireOp",EDGE,"E18.sketch_text.stroke-155"),sQuery(id+"F14.wireOp",EDGE,"E18.sketch_text.stroke-156"),sQuery(id+"F14.wireOp",EDGE,"E18.sketch_text.stroke-157"),sQuery(id+"F14.wireOp",EDGE,"E18.sketch_text.stroke-158"),sQuery(id+"F14.wireOp",EDGE,"E18.sketch_text.stroke-159"),sQuery(id+"F14.wireOp",EDGE,"E18.sketch_text.stroke-160"),sQuery(id+"F14.wireOp",EDGE,"E18.sketch_text.stroke-161"),sQuery(id+"F14.wireOp",EDGE,"E18.sketch_text.stroke-162"),sQuery(id+"F14.wireOp",EDGE,"E18.sketch_text.stroke-163"),sQuery(id+"F14.wireOp",EDGE,"E18.sketch_text.stroke-164"),sQuery(id+"F14.wireOp",EDGE,"E18.sketch_text.stroke-165"),sQuery(id+"F14.wireOp",EDGE,"E18.sketch_text.stroke-166"),sQuery(id+"F14.wireOp",EDGE,"E18.sketch_text.stroke-167"),sQuery(id+"F14.wireOp",EDGE,"E18.sketch_text.stroke-168"),sQuery(id+"F14.wireOp",EDGE,"E18.sketch_text.stroke-169"),sQuery(id+"F14.wireOp",EDGE,"E18.sketch_text.stroke-170"),sQuery(id+"F14.wireOp",EDGE,"E18.sketch_text.stroke-171"),sQuery(id+"F14.wireOp",EDGE,"E18.sketch_text.stroke-172"),sQuery(id+"F14.wireOp",EDGE,"E18.sketch_text.stroke-173"),sQuery(id+"F14.wireOp",EDGE,"E18.sketch_text.stroke-174"),sQuery(id+"F14.wireOp",EDGE,"E18.sketch_text.stroke-175"),sQuery(id+"F14.wireOp",EDGE,"E18.sketch_text.stroke-176"),sQuery(id+"F14.wireOp",EDGE,"E18.sketch_text.stroke-177"),sQuery(id+"F14.wireOp",EDGE,"E18.sketch_text.stroke-178"),sQuery(id+"F14.wireOp",EDGE,"E18.sketch_text.stroke-179"),sQuery(id+"F14.wireOp",EDGE,"E18.sketch_text.stroke-180"),sQuery(id+"F14.wireOp",EDGE,"E18.sketch_text.stroke-181"),sQuery(id+"F14.wireOp",EDGE,"E18.sketch_text.stroke-182")])],"isStart":false});
            var sketch = newSketch(context, id + "F18", { "sketchPlane" : qUnion([Q0])});
            skText(sketch, "E20", { "text": "9V", "fontName": "AllertaStencil-Regular.ttf"});
            const initialGuessF18  = {"E20": [-0.00689, 0.03875, 1, 0, 0.0072]};
            skSetInitialGuess(sketch, initialGuessF18);
            skSolve(sketch);
        }
        {
            var Q0;
            Q0 = qSketchRegion(id + "F18", true);
            extrude(context, id + "F19", {"entities" : qUnion([Q0]), "operationType" : NewBodyOperationType.ADD, "depth" : 1.27 * mm});
        }
        {
            var Q0;
            Q0=makeQuery(id+"F15.opExtrude","CAP_FACE",FACE,{"disambiguationData":[OSD([sQuery(id+"F0.wireOp",EDGE,"E0.bottom"),sQuery(id+"F0.wireOp",EDGE,"E0.top"),sQuery(id+"F0.wireOp",EDGE,"E0.left"),sQuery(id+"F14.wireOp",EDGE,"E18.sketch_text.stroke-0"),sQuery(id+"F14.wireOp",EDGE,"E18.sketch_text.stroke-1"),sQuery(id+"F14.wireOp",EDGE,"E18.sketch_text.stroke-2"),sQuery(id+"F14.wireOp",EDGE,"E18.sketch_text.stroke-3"),sQuery(id+"F14.wireOp",EDGE,"E18.sketch_text.stroke-4"),sQuery(id+"F14.wireOp",EDGE,"E18.sketch_text.stroke-5"),sQuery(id+"F14.wireOp",EDGE,"E18.sketch_text.stroke-6"),sQuery(id+"F14.wireOp",EDGE,"E18.sketch_text.stroke-7"),sQuery(id+"F14.wireOp",EDGE,"E18.sketch_text.stroke-8"),sQuery(id+"F14.wireOp",EDGE,"E18.sketch_text.stroke-9"),sQuery(id+"F14.wireOp",EDGE,"E18.sketch_text.stroke-10"),sQuery(id+"F14.wireOp",EDGE,"E18.sketch_text.stroke-11"),sQuery(id+"F14.wireOp",EDGE,"E18.sketch_text.stroke-12"),sQuery(id+"F14.wireOp",EDGE,"E18.sketch_text.stroke-13"),sQuery(id+"F14.wireOp",EDGE,"E18.sketch_text.stroke-14"),sQuery(id+"F14.wireOp",EDGE,"E18.sketch_text.stroke-15"),sQuery(id+"F14.wireOp",EDGE,"E18.sketch_text.stroke-16"),sQuery(id+"F14.wireOp",EDGE,"E18.sketch_text.stroke-17"),sQuery(id+"F14.wireOp",EDGE,"E18.sketch_text.stroke-18"),sQuery(id+"F14.wireOp",EDGE,"E18.sketch_text.stroke-19"),sQuery(id+"F14.wireOp",EDGE,"E18.sketch_text.stroke-20"),sQuery(id+"F14.wireOp",EDGE,"E18.sketch_text.stroke-21"),sQuery(id+"F14.wireOp",EDGE,"E18.sketch_text.stroke-22"),sQuery(id+"F14.wireOp",EDGE,"E18.sketch_text.stroke-23"),sQuery(id+"F14.wireOp",EDGE,"E18.sketch_text.stroke-24"),sQuery(id+"F14.wireOp",EDGE,"E18.sketch_text.stroke-25"),sQuery(id+"F14.wireOp",EDGE,"E18.sketch_text.stroke-26"),sQuery(id+"F14.wireOp",EDGE,"E18.sketch_text.stroke-27"),sQuery(id+"F14.wireOp",EDGE,"E18.sketch_text.stroke-28"),sQuery(id+"F14.wireOp",EDGE,"E18.sketch_text.stroke-29"),sQuery(id+"F14.wireOp",EDGE,"E18.sketch_text.stroke-30"),sQuery(id+"F14.wireOp",EDGE,"E18.sketch_text.stroke-31"),sQuery(id+"F14.wireOp",EDGE,"E18.sketch_text.stroke-32"),sQuery(id+"F14.wireOp",EDGE,"E18.sketch_text.stroke-33"),sQuery(id+"F14.wireOp",EDGE,"E18.sketch_text.stroke-34"),sQuery(id+"F14.wireOp",EDGE,"E18.sketch_text.stroke-35"),sQuery(id+"F14.wireOp",EDGE,"E18.sketch_text.stroke-36"),sQuery(id+"F14.wireOp",EDGE,"E18.sketch_text.stroke-37"),sQuery(id+"F14.wireOp",EDGE,"E18.sketch_text.stroke-38"),sQuery(id+"F14.wireOp",EDGE,"E18.sketch_text.stroke-39"),sQuery(id+"F14.wireOp",EDGE,"E18.sketch_text.stroke-40"),sQuery(id+"F14.wireOp",EDGE,"E18.sketch_text.stroke-41"),sQuery(id+"F14.wireOp",EDGE,"E18.sketch_text.stroke-42"),sQuery(id+"F14.wireOp",EDGE,"E18.sketch_text.stroke-43"),sQuery(id+"F14.wireOp",EDGE,"E18.sketch_text.stroke-44"),sQuery(id+"F14.wireOp",EDGE,"E18.sketch_text.stroke-45"),sQuery(id+"F14.wireOp",EDGE,"E18.sketch_text.stroke-46"),sQuery(id+"F14.wireOp",EDGE,"E18.sketch_text.stroke-47"),sQuery(id+"F14.wireOp",EDGE,"E18.sketch_text.stroke-48"),sQuery(id+"F14.wireOp",EDGE,"E18.sketch_text.stroke-49"),sQuery(id+"F14.wireOp",EDGE,"E18.sketch_text.stroke-50"),sQuery(id+"F14.wireOp",EDGE,"E18.sketch_text.stroke-51"),sQuery(id+"F14.wireOp",EDGE,"E18.sketch_text.stroke-52"),sQuery(id+"F14.wireOp",EDGE,"E18.sketch_text.stroke-53"),sQuery(id+"F14.wireOp",EDGE,"E18.sketch_text.stroke-54"),sQuery(id+"F14.wireOp",EDGE,"E18.sketch_text.stroke-55"),sQuery(id+"F14.wireOp",EDGE,"E18.sketch_text.stroke-56"),sQuery(id+"F14.wireOp",EDGE,"E18.sketch_text.stroke-57"),sQuery(id+"F14.wireOp",EDGE,"E18.sketch_text.stroke-58"),sQuery(id+"F14.wireOp",EDGE,"E18.sketch_text.stroke-59"),sQuery(id+"F14.wireOp",EDGE,"E18.sketch_text.stroke-60"),sQuery(id+"F14.wireOp",EDGE,"E18.sketch_text.stroke-61"),sQuery(id+"F14.wireOp",EDGE,"E18.sketch_text.stroke-62"),sQuery(id+"F14.wireOp",EDGE,"E18.sketch_text.stroke-63"),sQuery(id+"F14.wireOp",EDGE,"E18.sketch_text.stroke-64"),sQuery(id+"F14.wireOp",EDGE,"E18.sketch_text.stroke-65"),sQuery(id+"F14.wireOp",EDGE,"E18.sketch_text.stroke-66"),sQuery(id+"F14.wireOp",EDGE,"E18.sketch_text.stroke-67"),sQuery(id+"F14.wireOp",EDGE,"E18.sketch_text.stroke-68"),sQuery(id+"F14.wireOp",EDGE,"E18.sketch_text.stroke-69"),sQuery(id+"F14.wireOp",EDGE,"E18.sketch_text.stroke-70"),sQuery(id+"F14.wireOp",EDGE,"E18.sketch_text.stroke-71"),sQuery(id+"F14.wireOp",EDGE,"E18.sketch_text.stroke-72"),sQuery(id+"F14.wireOp",EDGE,"E18.sketch_text.stroke-73"),sQuery(id+"F14.wireOp",EDGE,"E18.sketch_text.stroke-74"),sQuery(id+"F14.wireOp",EDGE,"E18.sketch_text.stroke-75"),sQuery(id+"F14.wireOp",EDGE,"E18.sketch_text.stroke-76"),sQuery(id+"F14.wireOp",EDGE,"E18.sketch_text.stroke-77"),sQuery(id+"F14.wireOp",EDGE,"E18.sketch_text.stroke-78"),sQuery(id+"F14.wireOp",EDGE,"E18.sketch_text.stroke-79"),sQuery(id+"F14.wireOp",EDGE,"E18.sketch_text.stroke-80"),sQuery(id+"F14.wireOp",EDGE,"E18.sketch_text.stroke-81"),sQuery(id+"F14.wireOp",EDGE,"E18.sketch_text.stroke-82"),sQuery(id+"F14.wireOp",EDGE,"E18.sketch_text.stroke-83"),sQuery(id+"F14.wireOp",EDGE,"E18.sketch_text.stroke-84"),sQuery(id+"F14.wireOp",EDGE,"E18.sketch_text.stroke-85"),sQuery(id+"F14.wireOp",EDGE,"E18.sketch_text.stroke-86"),sQuery(id+"F14.wireOp",EDGE,"E18.sketch_text.stroke-87"),sQuery(id+"F14.wireOp",EDGE,"E18.sketch_text.stroke-88"),sQuery(id+"F14.wireOp",EDGE,"E18.sketch_text.stroke-89"),sQuery(id+"F14.wireOp",EDGE,"E18.sketch_text.stroke-90"),sQuery(id+"F14.wireOp",EDGE,"E18.sketch_text.stroke-91"),sQuery(id+"F14.wireOp",EDGE,"E18.sketch_text.stroke-92"),sQuery(id+"F14.wireOp",EDGE,"E18.sketch_text.stroke-93"),sQuery(id+"F14.wireOp",EDGE,"E18.sketch_text.stroke-94"),sQuery(id+"F14.wireOp",EDGE,"E18.sketch_text.stroke-95"),sQuery(id+"F14.wireOp",EDGE,"E18.sketch_text.stroke-96"),sQuery(id+"F14.wireOp",EDGE,"E18.sketch_text.stroke-97"),sQuery(id+"F14.wireOp",EDGE,"E18.sketch_text.stroke-98"),sQuery(id+"F14.wireOp",EDGE,"E18.sketch_text.stroke-99"),sQuery(id+"F14.wireOp",EDGE,"E18.sketch_text.stroke-100"),sQuery(id+"F14.wireOp",EDGE,"E18.sketch_text.stroke-101"),sQuery(id+"F14.wireOp",EDGE,"E18.sketch_text.stroke-102"),sQuery(id+"F14.wireOp",EDGE,"E18.sketch_text.stroke-103"),sQuery(id+"F14.wireOp",EDGE,"E18.sketch_text.stroke-104"),sQuery(id+"F14.wireOp",EDGE,"E18.sketch_text.stroke-105"),sQuery(id+"F14.wireOp",EDGE,"E18.sketch_text.stroke-106"),sQuery(id+"F14.wireOp",EDGE,"E18.sketch_text.stroke-107"),sQuery(id+"F14.wireOp",EDGE,"E18.sketch_text.stroke-108"),sQuery(id+"F14.wireOp",EDGE,"E18.sketch_text.stroke-109"),sQuery(id+"F14.wireOp",EDGE,"E18.sketch_text.stroke-110"),sQuery(id+"F14.wireOp",EDGE,"E18.sketch_text.stroke-111"),sQuery(id+"F14.wireOp",EDGE,"E18.sketch_text.stroke-112"),sQuery(id+"F14.wireOp",EDGE,"E18.sketch_text.stroke-113"),sQuery(id+"F14.wireOp",EDGE,"E18.sketch_text.stroke-114"),sQuery(id+"F14.wireOp",EDGE,"E18.sketch_text.stroke-115"),sQuery(id+"F14.wireOp",EDGE,"E18.sketch_text.stroke-116"),sQuery(id+"F14.wireOp",EDGE,"E18.sketch_text.stroke-117"),sQuery(id+"F14.wireOp",EDGE,"E18.sketch_text.stroke-118"),sQuery(id+"F14.wireOp",EDGE,"E18.sketch_text.stroke-119"),sQuery(id+"F14.wireOp",EDGE,"E18.sketch_text.stroke-120"),sQuery(id+"F14.wireOp",EDGE,"E18.sketch_text.stroke-121"),sQuery(id+"F14.wireOp",EDGE,"E18.sketch_text.stroke-122"),sQuery(id+"F14.wireOp",EDGE,"E18.sketch_text.stroke-123"),sQuery(id+"F14.wireOp",EDGE,"E18.sketch_text.stroke-124"),sQuery(id+"F14.wireOp",EDGE,"E18.sketch_text.stroke-125"),sQuery(id+"F14.wireOp",EDGE,"E18.sketch_text.stroke-126"),sQuery(id+"F14.wireOp",EDGE,"E18.sketch_text.stroke-127"),sQuery(id+"F14.wireOp",EDGE,"E18.sketch_text.stroke-128"),sQuery(id+"F14.wireOp",EDGE,"E18.sketch_text.stroke-129"),sQuery(id+"F14.wireOp",EDGE,"E18.sketch_text.stroke-130"),sQuery(id+"F14.wireOp",EDGE,"E18.sketch_text.stroke-131"),sQuery(id+"F14.wireOp",EDGE,"E18.sketch_text.stroke-132"),sQuery(id+"F14.wireOp",EDGE,"E18.sketch_text.stroke-133"),sQuery(id+"F14.wireOp",EDGE,"E18.sketch_text.stroke-134"),sQuery(id+"F14.wireOp",EDGE,"E18.sketch_text.stroke-135"),sQuery(id+"F14.wireOp",EDGE,"E18.sketch_text.stroke-136"),sQuery(id+"F14.wireOp",EDGE,"E18.sketch_text.stroke-137"),sQuery(id+"F14.wireOp",EDGE,"E18.sketch_text.stroke-138"),sQuery(id+"F14.wireOp",EDGE,"E18.sketch_text.stroke-139"),sQuery(id+"F14.wireOp",EDGE,"E18.sketch_text.stroke-140"),sQuery(id+"F14.wireOp",EDGE,"E18.sketch_text.stroke-141"),sQuery(id+"F14.wireOp",EDGE,"E18.sketch_text.stroke-142"),sQuery(id+"F14.wireOp",EDGE,"E18.sketch_text.stroke-143"),sQuery(id+"F14.wireOp",EDGE,"E18.sketch_text.stroke-144"),sQuery(id+"F14.wireOp",EDGE,"E18.sketch_text.stroke-145"),sQuery(id+"F14.wireOp",EDGE,"E18.sketch_text.stroke-146"),sQuery(id+"F14.wireOp",EDGE,"E18.sketch_text.stroke-147"),sQuery(id+"F14.wireOp",EDGE,"E18.sketch_text.stroke-148"),sQuery(id+"F14.wireOp",EDGE,"E18.sketch_text.stroke-149"),sQuery(id+"F14.wireOp",EDGE,"E18.sketch_text.stroke-150"),sQuery(id+"F14.wireOp",EDGE,"E18.sketch_text.stroke-151"),sQuery(id+"F14.wireOp",EDGE,"E18.sketch_text.stroke-152"),sQuery(id+"F14.wireOp",EDGE,"E18.sketch_text.stroke-153"),sQuery(id+"F14.wireOp",EDGE,"E18.sketch_text.stroke-154"),sQuery(id+"F14.wireOp",EDGE,"E18.sketch_text.stroke-155"),sQuery(id+"F14.wireOp",EDGE,"E18.sketch_text.stroke-156"),sQuery(id+"F14.wireOp",EDGE,"E18.sketch_text.stroke-157"),sQuery(id+"F14.wireOp",EDGE,"E18.sketch_text.stroke-158"),sQuery(id+"F14.wireOp",EDGE,"E18.sketch_text.stroke-159"),sQuery(id+"F14.wireOp",EDGE,"E18.sketch_text.stroke-160"),sQuery(id+"F14.wireOp",EDGE,"E18.sketch_text.stroke-161"),sQuery(id+"F14.wireOp",EDGE,"E18.sketch_text.stroke-162"),sQuery(id+"F14.wireOp",EDGE,"E18.sketch_text.stroke-163"),sQuery(id+"F14.wireOp",EDGE,"E18.sketch_text.stroke-164"),sQuery(id+"F14.wireOp",EDGE,"E18.sketch_text.stroke-165"),sQuery(id+"F14.wireOp",EDGE,"E18.sketch_text.stroke-166"),sQuery(id+"F14.wireOp",EDGE,"E18.sketch_text.stroke-167"),sQuery(id+"F14.wireOp",EDGE,"E18.sketch_text.stroke-168"),sQuery(id+"F14.wireOp",EDGE,"E18.sketch_text.stroke-169"),sQuery(id+"F14.wireOp",EDGE,"E18.sketch_text.stroke-170"),sQuery(id+"F14.wireOp",EDGE,"E18.sketch_text.stroke-171"),sQuery(id+"F14.wireOp",EDGE,"E18.sketch_text.stroke-172"),sQuery(id+"F14.wireOp",EDGE,"E18.sketch_text.stroke-173"),sQuery(id+"F14.wireOp",EDGE,"E18.sketch_text.stroke-174"),sQuery(id+"F14.wireOp",EDGE,"E18.sketch_text.stroke-175"),sQuery(id+"F14.wireOp",EDGE,"E18.sketch_text.stroke-176"),sQuery(id+"F14.wireOp",EDGE,"E18.sketch_text.stroke-177"),sQuery(id+"F14.wireOp",EDGE,"E18.sketch_text.stroke-178"),sQuery(id+"F14.wireOp",EDGE,"E18.sketch_text.stroke-179"),sQuery(id+"F14.wireOp",EDGE,"E18.sketch_text.stroke-180"),sQuery(id+"F14.wireOp",EDGE,"E18.sketch_text.stroke-181"),sQuery(id+"F14.wireOp",EDGE,"E18.sketch_text.stroke-182")])],"isStart":false});
            var sketch = newSketch(context, id + "F20", { "sketchPlane" : qUnion([Q0])});
            skText(sketch, "E21", { "text": "Battery", "fontName": "AllertaStencil-Regular.ttf"});
            const initialGuessF20  = {"E21": [-0.01033, 0.02632, 1, 0, 0.00401]};
            skSetInitialGuess(sketch, initialGuessF20);
            skSolve(sketch);
        }
        {
            var Q0;
            Q0 = qSketchRegion(id + "F20", true);
            extrude(context, id + "F21", {"entities" : qUnion([Q0]), "operationType" : NewBodyOperationType.ADD, "depth" : 0.74 * mm});
        }
        {
            var Q0;
            Q0=makeQuery(id+"F15.opExtrude","CAP_EDGE",EDGE,{"disambiguationData":[OSD([sQuery(id+"F0.wireOp",EDGE,"E0.bottom"),sQuery(id+"F0.wireOp",EDGE,"E0.left")])],"isStart":false});
            var Q1;
            Q1=makeQuery(id+"F1.opExtrude","SWEPT_EDGE",EDGE,{"disambiguationData":[OSD([sQuery(id+"F0.wireOp",EDGE,"E0.bottom"),sQuery(id+"F0.wireOp",EDGE,"E0.right")])]});
            var Q2;
            Q2=makeQuery(id+"F1.opExtrude","SWEPT_EDGE",EDGE,{"disambiguationData":[OSD([sQuery(id+"F0.wireOp",EDGE,"E0.top"),sQuery(id+"F0.wireOp",EDGE,"E0.right")])]});
            var Q3;
            Q3=makeQuery(id+"F15.opExtrude","CAP_EDGE",EDGE,{"disambiguationData":[OSD([sQuery(id+"F0.wireOp",EDGE,"E0.top"),sQuery(id+"F0.wireOp",EDGE,"E0.left")])],"isStart":false});
            fillet(context, id + "F22", {"entities" : qUnion([Q0, Q1, Q2, Q3]), "radius" : 5.08 * mm, "tangentPropagation" : true, "allowEdgeOverflow" : false});
        }
        {
            var Q0;
            Q0=makeQuery(id+"F2.imprint","IMPRINT",FACE,{"disambiguationData":[TD([[makeQuery(id+"F2.imprint","IMPRINT",EDGE,{"derivedFrom":sQuery(id+"F2.wireOp",EDGE,"E1")}),-1.0]])]});
            var sketch = newSketch(context, id + "F23", { "sketchPlane" : qUnion([Q0])});
            skLineSegment(sketch, "E22.bottom", {"start": v(-10.3, 16.66) * mm, "end": v(10.3, 16.66) * mm});
            skLineSegment(sketch, "E22.top", {"start": v(-10.3, -16.66) * mm, "end": v(10.3, -16.66) * mm});
            skLineSegment(sketch, "E22.left", {"start": v(-10.3, 16.66) * mm, "end": v(-10.3, -16.66) * mm});
            skLineSegment(sketch, "E22.right", {"start": v(10.3, 16.66) * mm, "end": v(10.3, -16.66) * mm});
            skPoint(sketch, "E22.middle", {"position": v(0, 0) * mm});
            skSolve(sketch);
        }
        {
            var Q0;
            Q0=makeQuery(id+"F23.imprint","IMPRINT",FACE,{"disambiguationData":[TD([[makeQuery(id+"F23.imprint","IMPRINT",EDGE,{"derivedFrom":sQuery(id+"F23.wireOp",EDGE,"E22.bottom")}),-1.0]])]});
            var Q1;
            Q1=makeQuery(id+"F5.boolean.opBoolean","COPY",FACE,{"derivedFrom":makeQuery(id+"F5.opExtrude","CAP_FACE",FACE,{"disambiguationData":[OSD([sQuery(id+"F4.wireOp",EDGE,"E8"),sQuery(id+"F4.wireOp",EDGE,"E9"),sQuery(id+"F4.wireOp",EDGE,"E10"),sQuery(id+"F4.wireOp",EDGE,"E11"),sQuery(id+"F4.wireOp",EDGE,"E12"),sQuery(id+"F4.wireOp",EDGE,"E13")])],"isStart":false})});
            extrude(context, id + "F24", {"entities" : qUnion([Q0, Q1]), "operationType" : NewBodyOperationType.ADD, "depth" : 0.25 * mm});
        }
        {
            var Q0;
            Q0=makeQuery(id+"F24.opExtrude","SWEPT_EDGE",EDGE,{"disambiguationData":[OSD([sQuery(id+"F23.wireOp",EDGE,"E22.bottom"),sQuery(id+"F23.wireOp",EDGE,"E22.left")])]});
            var Q1;
            Q1=makeQuery(id+"F24.opExtrude","SWEPT_EDGE",EDGE,{"disambiguationData":[OSD([sQuery(id+"F23.wireOp",EDGE,"E22.bottom"),sQuery(id+"F23.wireOp",EDGE,"E22.right")])]});
            var Q2;
            Q2=makeQuery(id+"F24.opExtrude","SWEPT_EDGE",EDGE,{"disambiguationData":[OSD([sQuery(id+"F23.wireOp",EDGE,"E22.top"),sQuery(id+"F23.wireOp",EDGE,"E22.right")])]});
            var Q3;
            Q3=makeQuery(id+"F24.opExtrude","SWEPT_EDGE",EDGE,{"disambiguationData":[OSD([sQuery(id+"F23.wireOp",EDGE,"E22.top"),sQuery(id+"F23.wireOp",EDGE,"E22.left")])]});
            fillet(context, id + "F25", {"entities" : qUnion([Q0, Q1, Q2, Q3]), "radius" : 5.08 * mm, "tangentPropagation" : true, "allowEdgeOverflow" : false});
        }
    });
